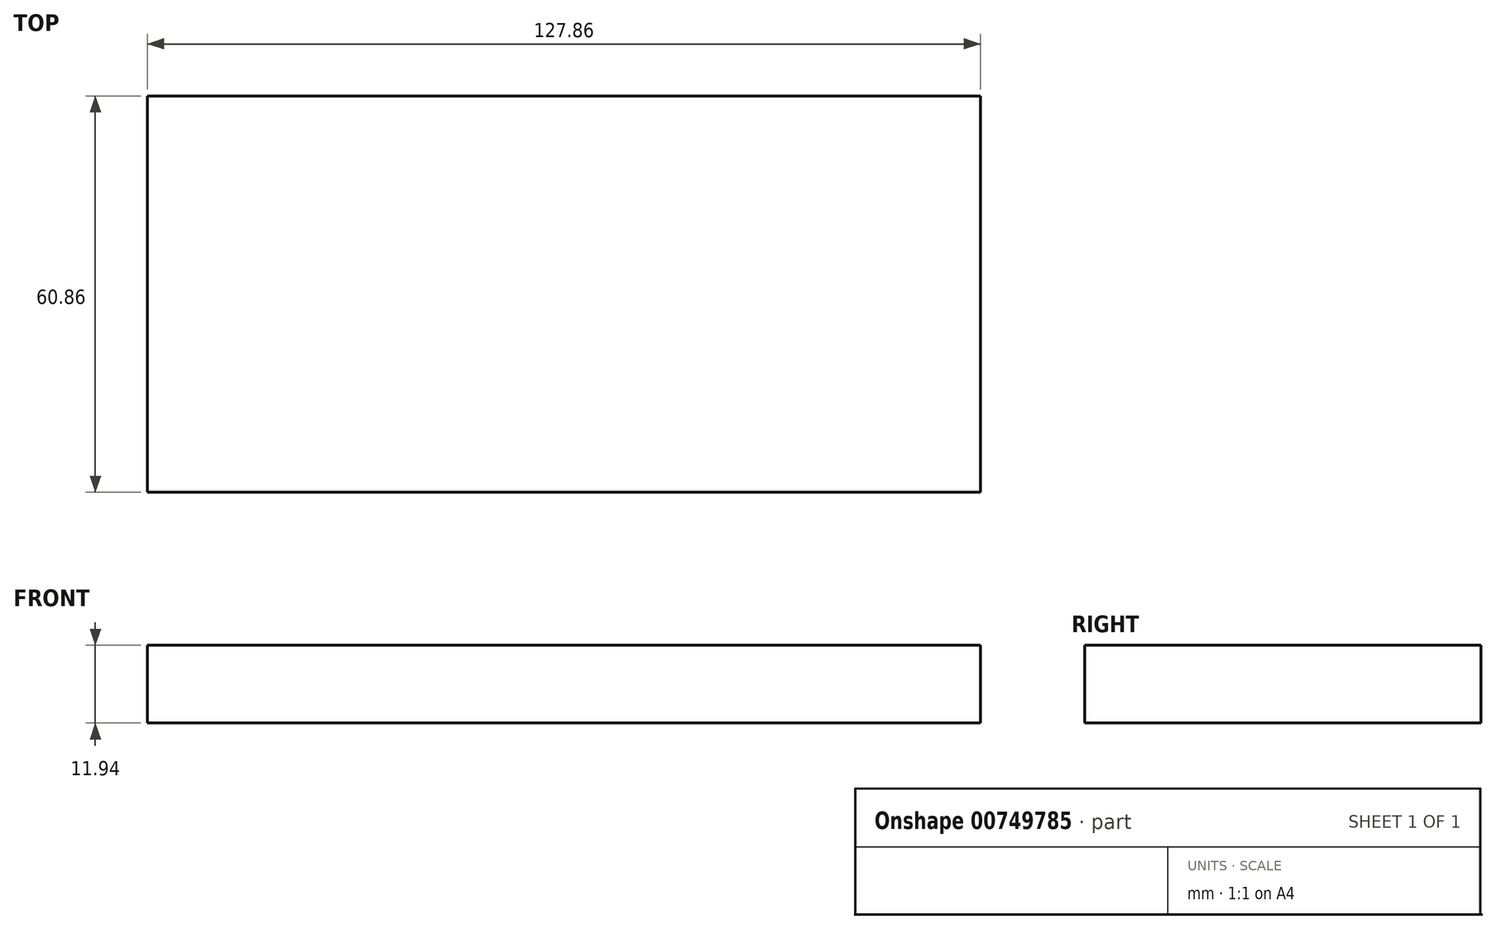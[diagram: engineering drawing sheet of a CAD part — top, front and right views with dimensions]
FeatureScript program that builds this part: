
annotation { "Feature Type Name" : "Feature", "Feature Type Description" : "" }
export const myFeature = defineFeature(function(context is Context, id is Id, definition is map)
    precondition{}
    {
        {
            var Q0;
            Q0=qCreatedBy(makeId("Top.planeOp"),FACE);
            var sketch = newSketch(context, id + "F0", { "sketchPlane" : qUnion([Q0])});
            skLineSegment(sketch, "E0.bottom", {"start": v(-76.44, 30.68) * mm, "end": v(51.42, 30.68) * mm});
            skLineSegment(sketch, "E0.top", {"start": v(-76.44, -30.18) * mm, "end": v(51.42, -30.18) * mm});
            skLineSegment(sketch, "E0.left", {"start": v(-76.44, 30.68) * mm, "end": v(-76.44, -30.18) * mm});
            skLineSegment(sketch, "E0.right", {"start": v(51.42, 30.68) * mm, "end": v(51.42, -30.18) * mm});
            skSolve(sketch);
        }
        {
            var Q0;
            Q0=makeQuery(id+"F0.imprint","IMPRINT",FACE,{"disambiguationData":[TD([[makeQuery(id+"F0.imprint","IMPRINT",EDGE,{"derivedFrom":sQuery(id+"F0.wireOp",EDGE,"E0.bottom")}),-1.0]])]});
            extrude(context, id + "F1", {"entities" : qUnion([Q0]), "depth" : 11.94 * mm, "offsetDistance" : 25.4 * mm});
        }
    });
